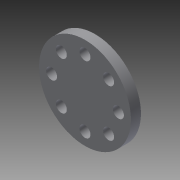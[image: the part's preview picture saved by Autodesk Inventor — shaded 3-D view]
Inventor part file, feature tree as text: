
AUTODESK INVENTOR PART (.ipt)
format: ipt  version: 2013 (Build 170138000, 138)  size: 99,328 bytes
history: native  units: mm
features: sketch x2, extrude x1, hole x1
ambient origin geometry x8: Origin, YZ Plane, XZ Plane, XY Plane, X Axis, Y Axis, Z Axis, Center Point
bodies: Solid1 (feature_tree)
feature tree (4):
  extrude  "Extrusion1"  Depth=6.0mm TaperAngle=0.0deg
  hole  "Hole1"  [1 undecoded]
  sketch  "Sketch1"  dims[d0=55.0mm d1=6.0mm d2=0.0mm]
  sketch  "Sketch2"  dims[d3=20.0mm d4=80.0mm d6=360.0deg d8=6.6mm d9=6.0mm d10=12.6mm d11=2.0mm d12=90.0deg d13=8.0mm d14=20.594885mm]
note: 1 required parameter value undecoded (feature->parameter linkage not recoverable at this tier; creation-order binding heuristic only, values carry confidence <= 0.55)
